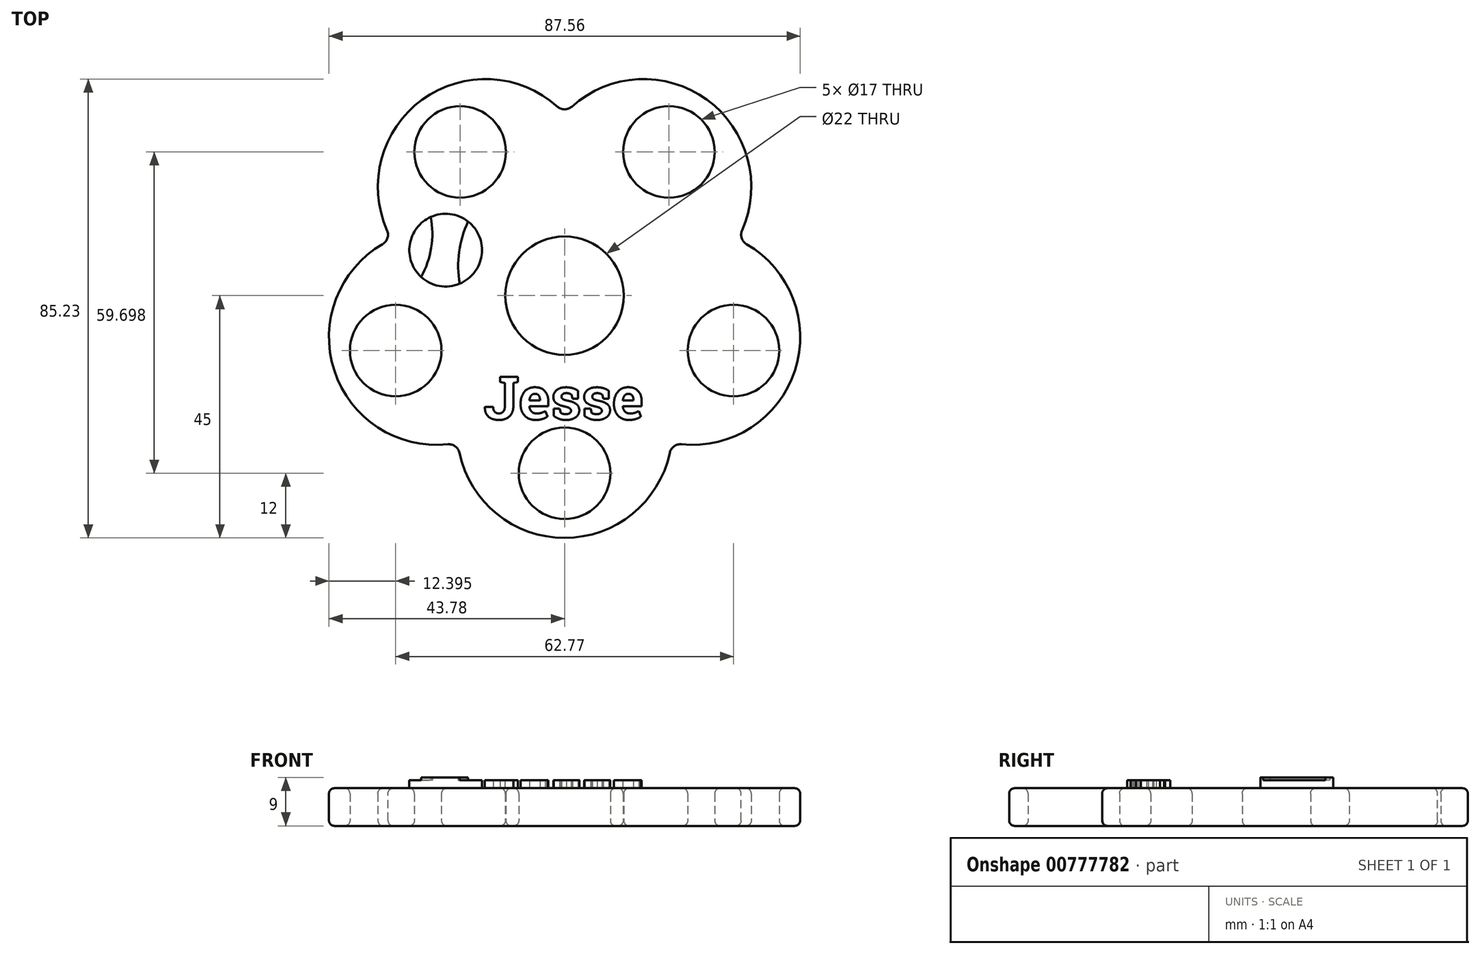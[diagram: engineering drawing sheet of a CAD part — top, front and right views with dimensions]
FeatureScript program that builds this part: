
annotation { "Feature Type Name" : "Feature", "Feature Type Description" : "" }
export const myFeature = defineFeature(function(context is Context, id is Id, definition is map)
    precondition{}
    {
        {
            var Q0;
            Q0=qCreatedBy(makeId("Top.planeOp"),FACE);
            var sketch = newSketch(context, id + "F0", { "sketchPlane" : qUnion([Q0])});
            skCircle(sketch, "E0.cCircle", {"center": v(0, 0) * mm, "radius": 25 * mm, "construction": true});
            skPoint(sketch, "E0.0.midPoint", {"position": v(14.7, 20.23) * mm});
            skArc(sketch, "E1", {"start": v(0, 33.8) * mm, "mid": v(-26.45, 36.4) * mm, "end": v(-32.14, 10.44) * mm});
            skArc(sketch, "E2", {"start": v(32.14, 10.44) * mm, "mid": v(26.45, 36.4) * mm, "end": v(0, 33.8) * mm});
            skArc(sketch, "E3", {"start": v(19.86, -27.34) * mm, "mid": v(42.8, -13.9) * mm, "end": v(32.14, 10.44) * mm});
            skArc(sketch, "E4", {"start": v(-19.86, -27.34) * mm, "mid": v(0, -45) * mm, "end": v(19.86, -27.34) * mm});
            skArc(sketch, "E5", {"start": v(-32.14, 10.44) * mm, "mid": v(-42.8, -13.9) * mm, "end": v(-19.86, -27.34) * mm});
            skCircle(sketch, "E6", {"center": v(0, 0) * mm, "radius": 33.8 * mm, "construction": true});
            skCircle(sketch, "E7", {"center": v(0, 0) * mm, "radius": 11 * mm});
            skCircle(sketch, "E8", {"center": v(-19.4, 26.7) * mm, "radius": 8.5 * mm});
            skCircle(sketch, "E9", {"center": v(19.4, 26.7) * mm, "radius": 8.5 * mm});
            skCircle(sketch, "E10", {"center": v(31.38, -10.2) * mm, "radius": 8.5 * mm});
            skCircle(sketch, "E11", {"center": v(0, -33) * mm, "radius": 8.5 * mm});
            skCircle(sketch, "E12", {"center": v(-31.38, -10.2) * mm, "radius": 8.5 * mm});
            skCircle(sketch, "E13", {"center": v(0, 0) * mm, "radius": 33 * mm, "construction": true});
            skLineSegment(sketch, "E14", {"start": v(0, 0) * mm, "end": v(0, 61.86) * mm, "construction": true});
            skLineSegment(sketch, "E15", {"start": v(0, 0) * mm, "end": v(38.47, 52.95) * mm, "construction": true});
            skLineSegment(sketch, "E16", {"start": v(0, 0) * mm, "end": v(76, -24.7) * mm, "construction": true});
            skLineSegment(sketch, "E17", {"start": v(0, 0) * mm, "end": v(0, -41.5) * mm, "construction": true});
            skLineSegment(sketch, "E18", {"start": v(0, 0) * mm, "end": v(-67.56, -21.95) * mm, "construction": true});
            skLineSegment(sketch, "E19", {"start": v(0, 0) * mm, "end": v(-35.13, 48.35) * mm, "construction": true});
            skSolve(sketch);
        }
        {
            var Q0;
            Q0=qSketchRegion(id+"F0",true);
            extrude(context, id + "F1", {"entities" : qUnion([Q0]), "depth" : 7 * mm, "offsetDistance" : 25.4 * mm});
        }
        {
            var Q0;
            Q0=makeQuery(id+"F1.opExtrude","SWEPT_EDGE",EDGE,{"disambiguationData":[OSD([sQuery(id+"F0.wireOp",EDGE,"E3"),sQuery(id+"F0.wireOp",EDGE,"E4")])]});
            var Q1;
            Q1=makeQuery(id+"F1.opExtrude","SWEPT_EDGE",EDGE,{"disambiguationData":[OSD([sQuery(id+"F0.wireOp",EDGE,"E2"),sQuery(id+"F0.wireOp",EDGE,"E3")])]});
            var Q2;
            Q2=makeQuery(id+"F1.opExtrude","SWEPT_EDGE",EDGE,{"disambiguationData":[OSD([sQuery(id+"F0.wireOp",EDGE,"E1"),sQuery(id+"F0.wireOp",EDGE,"E2")])]});
            var Q3;
            Q3=makeQuery(id+"F1.opExtrude","SWEPT_EDGE",EDGE,{"disambiguationData":[OSD([sQuery(id+"F0.wireOp",EDGE,"E1"),sQuery(id+"F0.wireOp",EDGE,"E5")])]});
            var Q4;
            Q4=makeQuery(id+"F1.opExtrude","SWEPT_EDGE",EDGE,{"disambiguationData":[OSD([sQuery(id+"F0.wireOp",EDGE,"E4"),sQuery(id+"F0.wireOp",EDGE,"E5")])]});
            fillet(context, id + "F2", {"entities" : qUnion([Q0, Q1, Q2, Q3, Q4]), "radius" : 2 * mm, "tangentPropagation" : true, "allowEdgeOverflow" : false});
        }
        {
            var Q0;
            Q0=makeQuery(id+"F1.opExtrude","CAP_FACE",FACE,{"disambiguationData":[OSD([sQuery(id+"F0.wireOp",EDGE,"E1"),sQuery(id+"F0.wireOp",EDGE,"E2"),sQuery(id+"F0.wireOp",EDGE,"E3"),sQuery(id+"F0.wireOp",EDGE,"E4"),sQuery(id+"F0.wireOp",EDGE,"E5"),sQuery(id+"F0.wireOp",EDGE,"E7"),sQuery(id+"F0.wireOp",EDGE,"E8"),sQuery(id+"F0.wireOp",EDGE,"E9"),sQuery(id+"F0.wireOp",EDGE,"E10"),sQuery(id+"F0.wireOp",EDGE,"E11"),sQuery(id+"F0.wireOp",EDGE,"E12")])],"isStart":false});
            var Q1;
            Q1=makeQuery(id+"F1.opExtrude","CAP_FACE",FACE,{"disambiguationData":[OSD([sQuery(id+"F0.wireOp",EDGE,"E1"),sQuery(id+"F0.wireOp",EDGE,"E2"),sQuery(id+"F0.wireOp",EDGE,"E3"),sQuery(id+"F0.wireOp",EDGE,"E4"),sQuery(id+"F0.wireOp",EDGE,"E5"),sQuery(id+"F0.wireOp",EDGE,"E7"),sQuery(id+"F0.wireOp",EDGE,"E8"),sQuery(id+"F0.wireOp",EDGE,"E9"),sQuery(id+"F0.wireOp",EDGE,"E10"),sQuery(id+"F0.wireOp",EDGE,"E11"),sQuery(id+"F0.wireOp",EDGE,"E12")])],"isStart":true});
            fillet(context, id + "F3", {"entities" : qUnion([Q0, Q1]), "radius" : 1 * mm, "tangentPropagation" : true, "allowEdgeOverflow" : false});
        }
        {
            var Q0;
            Q0=makeQuery(id+"F1.opExtrude","CAP_FACE",FACE,{"disambiguationData":[OSD([sQuery(id+"F0.wireOp",EDGE,"E1"),sQuery(id+"F0.wireOp",EDGE,"E2"),sQuery(id+"F0.wireOp",EDGE,"E3"),sQuery(id+"F0.wireOp",EDGE,"E4"),sQuery(id+"F0.wireOp",EDGE,"E5"),sQuery(id+"F0.wireOp",EDGE,"E7"),sQuery(id+"F0.wireOp",EDGE,"E8"),sQuery(id+"F0.wireOp",EDGE,"E9"),sQuery(id+"F0.wireOp",EDGE,"E10"),sQuery(id+"F0.wireOp",EDGE,"E11"),sQuery(id+"F0.wireOp",EDGE,"E12")])],"isStart":false});
            var sketch = newSketch(context, id + "F4", { "sketchPlane" : qUnion([Q0])});
            skText(sketch, "E20", { "text": "Jesse", "fontName": "RobotoSlab-Bold.ttf"});
            skCircle(sketch, "E21", {"center": v(-22.09, 8.45) * mm, "radius": 6.75 * mm});
            const initialGuessF4  = {"E20": [-0.015, -0.02299, 1, 0, 0.008]};
            skSetInitialGuess(sketch, initialGuessF4);
            skSolve(sketch);
        }
        {
            var Q0;
            Q0=qSketchRegion(id+"F4",true);
            extrude(context, id + "F5", {"entities" : qUnion([Q0]), "operationType" : NewBodyOperationType.ADD, "depth" : 1.5 * mm, "offsetDistance" : 25 * mm});
        }
        {
            var Q0;
            Q0=makeQuery(id+"F5.opExtrude","CAP_FACE",FACE,{"disambiguationData":[OSD([sQuery(id+"F4.wireOp",EDGE,"E21")])],"isStart":false});
            var sketch = newSketch(context, id + "F6", { "sketchPlane" : qUnion([Q0])});
            skArc(sketch, "E22", {"start": v(-26.65, 3.47) * mm, "mid": v(-24.78, 8.88) * mm, "end": v(-24.88, 14.6) * mm});
            skArc(sketch, "E23", {"start": v(-17.93, 13.77) * mm, "mid": v(-19.6, 8.12) * mm, "end": v(-19.48, 2.22) * mm});
            skArc(sketch, "E24", {"start": v(-17.93, 13.77) * mm, "mid": v(-21.3, 15.16) * mm, "end": v(-24.88, 14.6) * mm});
            skArc(sketch, "E25", {"start": v(-26.65, 3.47) * mm, "mid": v(-23.25, 1.8) * mm, "end": v(-19.48, 2.22) * mm});
            skSolve(sketch);
        }
        {
            var Q0;
            Q0 = qSketchRegion(id + "F6", true);
            extrude(context, id + "F7", {"entities" : qUnion([Q0]), "operationType" : NewBodyOperationType.ADD, "depth" : .5 * mm, "offsetDistance" : 25 * mm});
        }
    });
